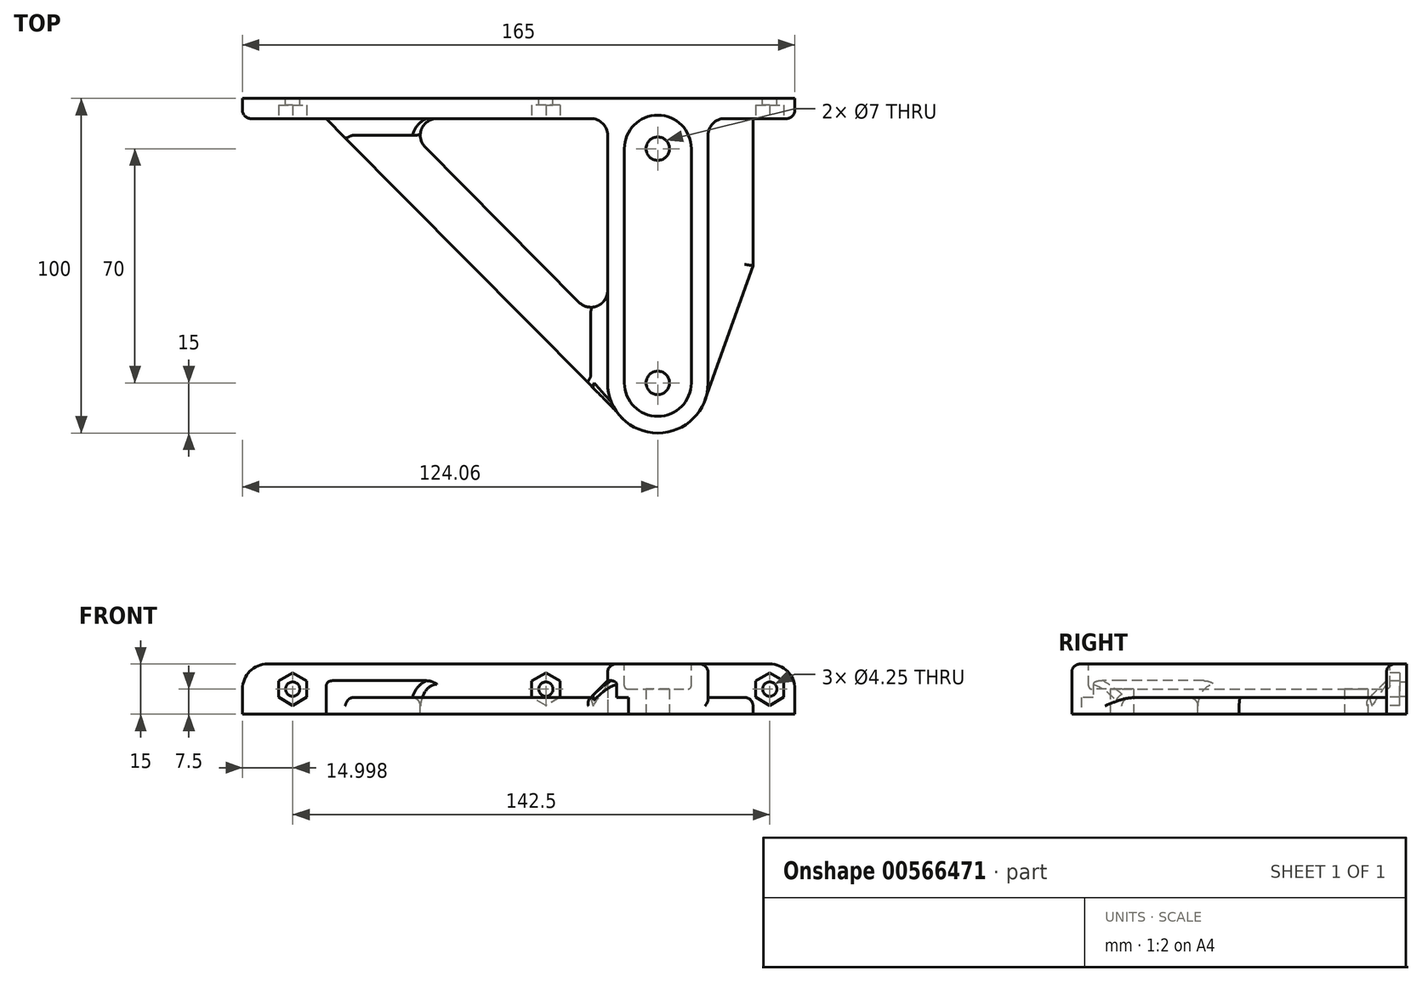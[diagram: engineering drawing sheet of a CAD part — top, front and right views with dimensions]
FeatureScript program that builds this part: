
annotation { "Feature Type Name" : "Feature", "Feature Type Description" : "" }
export const myFeature = defineFeature(function(context is Context, id is Id, definition is map)
    precondition{}
    {
        {
            var Q0;
            Q0=qCreatedBy(makeId("Top.planeOp"),FACE);
            var sketch = newSketch(context, id + "F0", { "sketchPlane" : qUnion([Q0])});
            skLineSegment(sketch, "E0", {"start": v(-124.06, 9) * mm, "end": v(-124.06, 15) * mm});
            skLineSegment(sketch, "E1", {"start": v(-124.06, 15) * mm, "end": v(40.94, 15) * mm});
            skLineSegment(sketch, "E2", {"start": v(40.94, 15) * mm, "end": v(40.94, 9) * mm});
            skLineSegment(sketch, "E3", {"start": v(12.37, -78.48) * mm, "end": v(10, -85) * mm, "construction": true});
            skLineSegment(sketch, "E4", {"start": v(10, -85) * mm, "end": v(-10, -85) * mm, "construction": true});
            skLineSegment(sketch, "E5", {"start": v(-10, -85) * mm, "end": v(-124.06, 0) * mm, "construction": true});
            skCircle(sketch, "E6", {"center": v(0, 0) * mm, "radius": 3.5 * mm});
            skCircle(sketch, "E7", {"center": v(0, -70) * mm, "radius": 3.5 * mm});
            skArc(sketch, "E8", {"start": v(-8.7, -82.22) * mm, "mid": v(4.5, -84.31) * mm, "end": v(14.13, -75.05) * mm});
            skLineSegment(sketch, "E9", {"start": v(28.44, -34.99) * mm, "end": v(14.13, -75.05) * mm});
            skLineSegment(sketch, "E10", {"start": v(-124.06, 0) * mm, "end": v(-8.7, -82.22) * mm, "construction": true});
            skLineSegment(sketch, "E11", {"start": v(-77.95, 9) * mm, "end": v(-15, 9) * mm});
            skLineSegment(sketch, "E12", {"start": v(-15, 9) * mm, "end": v(-15, -54.55) * mm});
            skLineSegment(sketch, "E13", {"start": v(-15, -54.55) * mm, "end": v(-77.95, 9) * mm});
            skLineSegment(sketch, "E14", {"start": v(-124.06, 9) * mm, "end": v(-99.06, 9) * mm});
            skLineSegment(sketch, "E15", {"start": v(-99.06, 9) * mm, "end": v(-8.7, -82.22) * mm});
            skLineSegment(sketch, "E16", {"start": v(28.44, 9) * mm, "end": v(40.94, 9) * mm});
            skLineSegment(sketch, "E17", {"start": v(28.44, 9) * mm, "end": v(28.44, -34.99) * mm});
            skPoint(sketch, "E18.orphan", {"position": v(40.94, 0) * mm});
            skSolve(sketch);
        }
        {
            var Q0;
            Q0=qSketchRegion(id+"F0",true);
            extrude(context, id + "F1", {"entities" : qUnion([Q0]), "depth" : 5 * mm});
        }
        {
            var Q0;
            Q0=makeQuery(id+"F1.opExtrude","CAP_FACE",FACE,{"disambiguationData":[OSD([sQuery(id+"F0.wireOp",EDGE,"E0"),sQuery(id+"F0.wireOp",EDGE,"E1"),sQuery(id+"F0.wireOp",EDGE,"E2"),sQuery(id+"F0.wireOp",EDGE,"E3"),sQuery(id+"F0.wireOp",EDGE,"E4"),sQuery(id+"F0.wireOp",EDGE,"E5"),sQuery(id+"F0.wireOp",EDGE,"E6"),sQuery(id+"F0.wireOp",EDGE,"E7"),sQuery(id+"F0.wireOp",EDGE,"brWuAORZ-QQ3N-mHyy-jjcm-9xjy5NoIPpaN"),sQuery(id+"F0.wireOp",EDGE,"hGYEL4FP-7Z2F-9BLv-NZoW-4O7jBzdm4NG0"),sQuery(id+"F0.wireOp",EDGE,"Ev3Ag6zw-3mFU-VTcE-mw61-bQwCWqHxOj75"),sQuery(id+"F0.wireOp",EDGE,"rvlW2tZY-N1AQ-Yf2F-EbRQ-ggfH0PUhPHp1")])],"isStart":false});
            var sketch = newSketch(context, id + "F2", { "sketchPlane" : qUnion([Q0])});
            skLineSegment(sketch, "E19.bottom", {"start": v(-124.06, 15) * mm, "end": v(40.94, 15) * mm});
            skLineSegment(sketch, "E19.top", {"start": v(-124.06, 9) * mm, "end": v(-15, 9) * mm});
            skLineSegment(sketch, "E19.left", {"start": v(-124.06, 15) * mm, "end": v(-124.06, 9) * mm});
            skLineSegment(sketch, "E19.right", {"start": v(40.94, 15) * mm, "end": v(40.94, 9) * mm});
            skLineSegment(sketch, "E20.left", {"start": v(-15, -70) * mm, "end": v(-15, 9) * mm});
            skLineSegment(sketch, "E20.right", {"start": v(15, -70) * mm, "end": v(15, 9) * mm});
            skLineSegment(sketch, "E21.trimOffspring", {"start": v(15, 9) * mm, "end": v(40.94, 9) * mm});
            skCircle(sketch, "E22", {"center": v(0, 0) * mm, "radius": 3.5 * mm});
            skCircle(sketch, "E23", {"center": v(0, -70) * mm, "radius": 3.5 * mm});
            skArc(sketch, "E24", {"start": v(0, -85) * mm, "mid": v(10.6, -80.6) * mm, "end": v(15, -70) * mm});
            skArc(sketch, "E25.MirrorCS", {"start": v(0, -85) * mm, "mid": v(-10.6, -80.6) * mm, "end": v(-15, -70) * mm});
            skSolve(sketch);
        }
        {
            var Q0;
            Q0=qSketchRegion(id+"F2",true);
            extrude(context, id + "F3", {"entities" : qUnion([Q0]), "operationType" : NewBodyOperationType.ADD, "depth" : 10 * mm});
        }
        {
            var Q0;
            Q0=makeQuery(id+"F3.opExtrude","SWEPT_EDGE",EDGE,{"disambiguationData":[OSD([sQuery(id+"F2.wireOp",EDGE,"E19.top"),sQuery(id+"F2.wireOp",EDGE,"E20.left")])]});
            var Q1;
            Q1=makeQuery(id+"F3.opExtrude","SWEPT_EDGE",EDGE,{"disambiguationData":[OSD([sQuery(id+"F2.wireOp",EDGE,"E20.right"),sQuery(id+"F2.wireOp",EDGE,"E21.trimOffspring")])]});
            fillet(context, id + "F4", {"entities" : qUnion([Q0, Q1]), "radius" : 5 * mm, "tangentPropagation" : true, "allowEdgeOverflow" : false});
        }
        {
            var Q0;
            Q0=makeQuery(id+"F3.boolean.opBoolean","MERGE",FACE,{"derivedFrom":[makeQuery(id+"F1.opExtrude","SWEPT_FACE",FACE,{"disambiguationData":[OSD([sQuery(id+"F0.wireOp",EDGE,"E1")])]}),makeQuery(id+"F3.opExtrude","SWEPT_FACE",FACE,{"disambiguationData":[OSD([sQuery(id+"F2.wireOp",EDGE,"E19.bottom")])]})]});
            var sketch = newSketch(context, id + "F5", { "sketchPlane" : qUnion([Q0])});
            skCircle(sketch, "E26", {"center": v(-33.44, 7.5) * mm, "radius": 2.12 * mm});
            skCircle(sketch, "E27", {"center": v(109.06, 7.5) * mm, "radius": 2.12 * mm});
            skCircle(sketch, "E28.MirrorC", {"center": v(33.44, 7.5) * mm, "radius": 2.12 * mm});
            skSolve(sketch);
        }
        {
            var Q0;
            Q0=qSketchRegion(id+"F5",true);
            extrude(context, id + "F6", {"entities" : qUnion([Q0]), "operationType" : NewBodyOperationType.REMOVE, "oppositeDirection" : true, "depth" : 25 * mm});
        }
        {
            var Q0;
            {var subQ0=sQuery(id+"F0.wireOp",EDGE,"Ev3Ag6zw-3mFU-VTcE-mw61-bQwCWqHxOj75");var subQ1=sQuery(id+"F0.wireOp",EDGE,"hGYEL4FP-7Z2F-9BLv-NZoW-4O7jBzdm4NG0");var subQ2=sQuery(id+"F0.wireOp",EDGE,"rvlW2tZY-N1AQ-Yf2F-EbRQ-ggfH0PUhPHp1");var subQ3=sQuery(id+"F0.wireOp",EDGE,"E0");var subQ4=sQuery(id+"F0.wireOp",EDGE,"E8");var subQ5=sQuery(id+"F0.wireOp",EDGE,"E10");var subQ6=sQuery(id+"F2.wireOp",EDGE,"E19.top");var subQ7=sQuery(id+"F2.wireOp",EDGE,"E20.left");Q0=makeQuery(id+"F4.opFillet","BLEND_EDGE",EDGE,{"blendedFrom":[makeQuery(id+"F3.opExtrude","SWEPT_EDGE",EDGE,{"disambiguationData":[OSD([subQ6,subQ7])]}),makeQuery(id+"F3.boolean.opBoolean","SPLIT",FACE,{"disambiguationData":[TD([makeQuery(id+"F1.opExtrude","SWEPT_FACE",FACE,{"disambiguationData":[OSD([subQ3])]})])],"derivedFrom":makeQuery(id+"F1.opExtrude","CAP_FACE",FACE,{"disambiguationData":[OSD([subQ3,sQuery(id+"F0.wireOp",EDGE,"E1"),sQuery(id+"F0.wireOp",EDGE,"E2"),sQuery(id+"F0.wireOp",EDGE,"E6"),sQuery(id+"F0.wireOp",EDGE,"E7"),sQuery(id+"F0.wireOp",EDGE,"brWuAORZ-QQ3N-mHyy-jjcm-9xjy5NoIPpaN"),subQ1,subQ0,subQ2,subQ4,sQuery(id+"F0.wireOp",EDGE,"E9"),subQ5])],"isStart":false})})],"blendedInto":[makeQuery(id+"F3.boolean.opBoolean","SPLIT",FACE,{"disambiguationData":[TD([makeQuery(id+"F1.opExtrude","SWEPT_FACE",FACE,{"disambiguationData":[OSD([subQ3])]})])],"derivedFrom":makeQuery(id+"F1.opExtrude","CAP_FACE",FACE,{"disambiguationData":[OSD([subQ3,sQuery(id+"F0.wireOp",EDGE,"E1"),sQuery(id+"F0.wireOp",EDGE,"E2"),sQuery(id+"F0.wireOp",EDGE,"E6"),sQuery(id+"F0.wireOp",EDGE,"E7"),sQuery(id+"F0.wireOp",EDGE,"brWuAORZ-QQ3N-mHyy-jjcm-9xjy5NoIPpaN"),subQ1,subQ0,subQ2,subQ4,sQuery(id+"F0.wireOp",EDGE,"E9"),subQ5])],"isStart":false})})]});}
            var Q1;
            {var subQ0=sQuery(id+"F0.wireOp",EDGE,"E8");var subQ1=sQuery(id+"F0.wireOp",EDGE,"E9");var subQ2=sQuery(id+"F0.wireOp",EDGE,"brWuAORZ-QQ3N-mHyy-jjcm-9xjy5NoIPpaN");var subQ3=sQuery(id+"F0.wireOp",EDGE,"E2");var subQ4=sQuery(id+"F2.wireOp",EDGE,"E20.right");var subQ5=sQuery(id+"F2.wireOp",EDGE,"E21.trimOffspring");Q1=makeQuery(id+"F4.opFillet","BLEND_EDGE",EDGE,{"blendedFrom":[makeQuery(id+"F3.opExtrude","SWEPT_EDGE",EDGE,{"disambiguationData":[OSD([subQ4,subQ5])]}),makeQuery(id+"F3.boolean.opBoolean","SPLIT",FACE,{"disambiguationData":[TD([makeQuery(id+"F1.opExtrude","SWEPT_FACE",FACE,{"disambiguationData":[OSD([subQ3])]})])],"derivedFrom":makeQuery(id+"F1.opExtrude","CAP_FACE",FACE,{"disambiguationData":[OSD([sQuery(id+"F0.wireOp",EDGE,"E0"),sQuery(id+"F0.wireOp",EDGE,"E1"),subQ3,sQuery(id+"F0.wireOp",EDGE,"E6"),sQuery(id+"F0.wireOp",EDGE,"E7"),subQ2,sQuery(id+"F0.wireOp",EDGE,"hGYEL4FP-7Z2F-9BLv-NZoW-4O7jBzdm4NG0"),sQuery(id+"F0.wireOp",EDGE,"Ev3Ag6zw-3mFU-VTcE-mw61-bQwCWqHxOj75"),sQuery(id+"F0.wireOp",EDGE,"rvlW2tZY-N1AQ-Yf2F-EbRQ-ggfH0PUhPHp1"),subQ0,subQ1,sQuery(id+"F0.wireOp",EDGE,"E10")])],"isStart":false})})],"blendedInto":[makeQuery(id+"F3.boolean.opBoolean","SPLIT",FACE,{"disambiguationData":[TD([makeQuery(id+"F1.opExtrude","SWEPT_FACE",FACE,{"disambiguationData":[OSD([subQ3])]})])],"derivedFrom":makeQuery(id+"F1.opExtrude","CAP_FACE",FACE,{"disambiguationData":[OSD([sQuery(id+"F0.wireOp",EDGE,"E0"),sQuery(id+"F0.wireOp",EDGE,"E1"),subQ3,sQuery(id+"F0.wireOp",EDGE,"E6"),sQuery(id+"F0.wireOp",EDGE,"E7"),subQ2,sQuery(id+"F0.wireOp",EDGE,"hGYEL4FP-7Z2F-9BLv-NZoW-4O7jBzdm4NG0"),sQuery(id+"F0.wireOp",EDGE,"Ev3Ag6zw-3mFU-VTcE-mw61-bQwCWqHxOj75"),sQuery(id+"F0.wireOp",EDGE,"rvlW2tZY-N1AQ-Yf2F-EbRQ-ggfH0PUhPHp1"),subQ0,subQ1,sQuery(id+"F0.wireOp",EDGE,"E10")])],"isStart":false})})]});}
            var Q2;
            Q2=makeQuery(id+"F3.opExtrude","CAP_EDGE",EDGE,{"disambiguationData":[OSD([sQuery(id+"F2.wireOp",EDGE,"E20.left")])],"isStart":true});
            var Q3;
            Q3=makeQuery(id+"F3.opExtrude","CAP_EDGE",EDGE,{"disambiguationData":[OSD([sQuery(id+"F2.wireOp",EDGE,"E19.top")])],"isStart":true});
            var Q4;
            Q4=makeQuery(id+"F3.opExtrude","CAP_EDGE",EDGE,{"disambiguationData":[OSD([sQuery(id+"F2.wireOp",EDGE,"E21.trimOffspring")])],"isStart":true});
            chamfer(context, id + "F7", {"entities" : qUnion([Q0, Q1, Q2, Q3, Q4]), "width" : 5 * mm, "tangentPropagation" : true});
        }
        {
            var Q0;
            Q0=makeQuery(id+"F1.opExtrude","SWEPT_EDGE",EDGE,{"disambiguationData":[OSD([sQuery(id+"F0.wireOp",EDGE,"E12"),sQuery(id+"F0.wireOp",EDGE,"E13")])]});
            var Q1;
            Q1=makeQuery(id+"F1.opExtrude","SWEPT_EDGE",EDGE,{"disambiguationData":[OSD([sQuery(id+"F0.wireOp",EDGE,"E11"),sQuery(id+"F0.wireOp",EDGE,"E12")])]});
            var Q2;
            Q2=makeQuery(id+"F1.opExtrude","SWEPT_EDGE",EDGE,{"disambiguationData":[OSD([sQuery(id+"F0.wireOp",EDGE,"E11"),sQuery(id+"F0.wireOp",EDGE,"E13")])]});
            fillet(context, id + "F8", {"entities" : qUnion([Q0, Q1, Q2]), "radius" : 5 * mm, "tangentPropagation" : true, "allowEdgeOverflow" : false});
        }
        {
            var Q0;
            Q0=makeQuery(id+"F3.opExtrude","CAP_FACE",FACE,{"disambiguationData":[OSD([sQuery(id+"F2.wireOp",EDGE,"E19.bottom"),sQuery(id+"F2.wireOp",EDGE,"E19.top"),sQuery(id+"F2.wireOp",EDGE,"E19.left"),sQuery(id+"F2.wireOp",EDGE,"E19.right"),sQuery(id+"F2.wireOp",EDGE,"E20.left"),sQuery(id+"F2.wireOp",EDGE,"E20.right"),sQuery(id+"F2.wireOp",EDGE,"E21.trimOffspring"),sQuery(id+"F2.wireOp",EDGE,"E22"),sQuery(id+"F2.wireOp",EDGE,"E23"),sQuery(id+"F2.wireOp",EDGE,"E24"),sQuery(id+"F2.wireOp",EDGE,"E25.MirrorCS")])],"isStart":false});
            var sketch = newSketch(context, id + "F9", { "sketchPlane" : qUnion([Q0])});
            skLineSegment(sketch, "E29.bottom", {"start": v(0, -80) * mm, "end": v(0, -80) * mm});
            skLineSegment(sketch, "E29.top", {"start": v(0, 10) * mm, "end": v(0, 10) * mm});
            skLineSegment(sketch, "E29.left", {"start": v(10, -70) * mm, "end": v(10, 0) * mm});
            skLineSegment(sketch, "E29.right", {"start": v(-10, -70) * mm, "end": v(-10, 0) * mm});
            skPoint(sketch, "E29.middle", {"position": v(0, -35) * mm});
            skPoint(sketch, "E30.visualSharp", {"position": v(-10, 10) * mm});
            skArc(sketch, "E30.filletArc", {"start": v(0, 10) * mm, "mid": v(-7.07, 7.07) * mm, "end": v(-10, 0) * mm});
            skPoint(sketch, "E31.visualSharp", {"position": v(10, 10) * mm});
            skArc(sketch, "E31.filletArc", {"start": v(10, 0) * mm, "mid": v(7.07, 7.07) * mm, "end": v(0, 10) * mm});
            skPoint(sketch, "E32.visualSharp", {"position": v(10, -80) * mm});
            skArc(sketch, "E32.filletArc", {"start": v(0, -80) * mm, "mid": v(7.07, -77.07) * mm, "end": v(10, -70) * mm});
            skPoint(sketch, "E33.visualSharp", {"position": v(-10, -80) * mm});
            skArc(sketch, "E33.filletArc", {"start": v(-10, -70) * mm, "mid": v(-7.07, -77.07) * mm, "end": v(0, -80) * mm});
            skSolve(sketch);
        }
        {
            var Q0;
            Q0=qSketchRegion(id+"F9",true);
            extrude(context, id + "F10", {"entities" : qUnion([Q0]), "operationType" : NewBodyOperationType.REMOVE, "oppositeDirection" : true, "depth" : 7.5 * mm});
        }
        {
            var Q0;
            Q0=makeQuery(id+"F3.opExtrude","CAP_EDGE",EDGE,{"disambiguationData":[OSD([sQuery(id+"F2.wireOp",EDGE,"E19.right")])],"isStart":false});
            var Q1;
            Q1=makeQuery(id+"F3.opExtrude","CAP_EDGE",EDGE,{"disambiguationData":[OSD([sQuery(id+"F2.wireOp",EDGE,"E19.left")])],"isStart":false});
            fillet(context, id + "F11", {"entities" : qUnion([Q0, Q1]), "radius" : 7.5 * mm, "tangentPropagation" : true, "allowEdgeOverflow" : false});
        }
        {
            var Q0;
            Q0=makeQuery(id+"F3.opExtrude","CAP_EDGE",EDGE,{"disambiguationData":[OSD([sQuery(id+"F2.wireOp",EDGE,"E20.left")])],"isStart":false});
            var Q1;
            Q1=makeQuery(id+"F1.opExtrude","CAP_EDGE",EDGE,{"disambiguationData":[OSD([sQuery(id+"F0.wireOp",EDGE,"E9")])],"isStart":false});
            var Q2;
            Q2=makeQuery(id+"F1.opExtrude","CAP_EDGE",EDGE,{"disambiguationData":[OSD([sQuery(id+"F0.wireOp",EDGE,"E17")])],"isStart":false});
            var Q3;
            {var subQ0=sQuery(id+"F0.wireOp",EDGE,"E15");Q3=makeQuery(id+"F3.boolean.opBoolean","SPLIT",EDGE,{"disambiguationData":[topologyDisambiguationEdgeConnected([makeQuery(id+"F1.opExtrude","CAP_FACE",FACE,{"disambiguationData":[OSD([sQuery(id+"F0.wireOp",EDGE,"E0"),sQuery(id+"F0.wireOp",EDGE,"E1"),sQuery(id+"F0.wireOp",EDGE,"E2"),sQuery(id+"F0.wireOp",EDGE,"E6"),sQuery(id+"F0.wireOp",EDGE,"E7"),sQuery(id+"F0.wireOp",EDGE,"E8"),sQuery(id+"F0.wireOp",EDGE,"E9"),sQuery(id+"F0.wireOp",EDGE,"E11"),sQuery(id+"F0.wireOp",EDGE,"E12"),sQuery(id+"F0.wireOp",EDGE,"E13"),sQuery(id+"F0.wireOp",EDGE,"E14"),subQ0,sQuery(id+"F0.wireOp",EDGE,"E16"),sQuery(id+"F0.wireOp",EDGE,"E17")])],"isStart":false})])],"derivedFrom":makeQuery(id+"F1.opExtrude","CAP_EDGE",EDGE,{"disambiguationData":[OSD([subQ0])],"isStart":false})});}
            var Q4;
            Q4=makeQuery(id+"F1.opExtrude","CAP_EDGE",EDGE,{"disambiguationData":[OSD([sQuery(id+"F0.wireOp",EDGE,"E13")])],"isStart":false});
            var Q5;
            Q5=makeQuery(id+"F10.boolean.opBoolean","COPY",EDGE,{"derivedFrom":makeQuery(id+"F10.opExtrude","CAP_EDGE",EDGE,{"disambiguationData":[OSD([sQuery(id+"F9.wireOp",EDGE,"E30.filletArc"),sQuery(id+"F9.wireOp",EDGE,"E31.filletArc")])],"isStart":true})});
            var Q6;
            Q6=makeQuery(id+"F7.opChamfer","BLEND_EDGE",EDGE,{"blendedFrom":[makeQuery(id+"F3.opExtrude","CAP_EDGE",EDGE,{"disambiguationData":[OSD([sQuery(id+"F2.wireOp",EDGE,"E19.top")])],"isStart":true}),makeQuery(id+"F1.opExtrude","SWEPT_FACE",FACE,{"disambiguationData":[OSD([sQuery(id+"F0.wireOp",EDGE,"E15")])]})],"blendedInto":[makeQuery(id+"F1.opExtrude","SWEPT_FACE",FACE,{"disambiguationData":[OSD([sQuery(id+"F0.wireOp",EDGE,"E15")])]})]});
            var Q7;
            Q7=makeQuery(id+"F8.opFillet","BLEND_EDGE",EDGE,{"blendedFrom":[makeQuery(id+"F1.opExtrude","SWEPT_EDGE",EDGE,{"disambiguationData":[OSD([sQuery(id+"F0.wireOp",EDGE,"E11"),sQuery(id+"F0.wireOp",EDGE,"E13")])]}),makeQuery(id+"F7.opChamfer","BLEND_FACE",FACE,{"disambiguationData":[OSD([sQuery(id+"F2.wireOp",EDGE,"E19.top")])]})],"blendedInto":[makeQuery(id+"F7.opChamfer","BLEND_FACE",FACE,{"disambiguationData":[OSD([sQuery(id+"F2.wireOp",EDGE,"E19.top")])]})]});
            var Q8;
            Q8=makeQuery(id+"F7.opChamfer","BLEND_EDGE",EDGE,{"blendedFrom":[makeQuery(id+"F3.opExtrude","CAP_EDGE",EDGE,{"disambiguationData":[OSD([sQuery(id+"F2.wireOp",EDGE,"E21.trimOffspring")])],"isStart":true}),makeQuery(id+"F1.opExtrude","SWEPT_FACE",FACE,{"disambiguationData":[OSD([sQuery(id+"F0.wireOp",EDGE,"E17")])]})],"blendedInto":[makeQuery(id+"F1.opExtrude","SWEPT_FACE",FACE,{"disambiguationData":[OSD([sQuery(id+"F0.wireOp",EDGE,"E17")])]})]});
            var Q9;
            {var subQ0=sQuery(id+"F0.wireOp",EDGE,"E15");var subQ1=makeQuery(id+"F1.opExtrude","SWEPT_FACE",FACE,{"disambiguationData":[OSD([subQ0])]});var subQ2=sQuery(id+"F0.wireOp",EDGE,"E12");var subQ3=sQuery(id+"F0.wireOp",EDGE,"E8");var subQ4=makeQuery(id+"F1.opExtrude","CAP_FACE",FACE,{"disambiguationData":[OSD([sQuery(id+"F0.wireOp",EDGE,"E0"),sQuery(id+"F0.wireOp",EDGE,"E1"),sQuery(id+"F0.wireOp",EDGE,"E2"),sQuery(id+"F0.wireOp",EDGE,"E6"),sQuery(id+"F0.wireOp",EDGE,"E7"),subQ3,sQuery(id+"F0.wireOp",EDGE,"E9"),sQuery(id+"F0.wireOp",EDGE,"E11"),subQ2,sQuery(id+"F0.wireOp",EDGE,"E13"),sQuery(id+"F0.wireOp",EDGE,"E14"),subQ0,sQuery(id+"F0.wireOp",EDGE,"E16"),sQuery(id+"F0.wireOp",EDGE,"E17")])],"isStart":false});var subQ5=sQuery(id+"F2.wireOp",EDGE,"E25.MirrorCS");var subQ6=sQuery(id+"F2.wireOp",EDGE,"E24");var subQ8=makeQuery(id+"F1.opExtrude","SWEPT_FACE",FACE,{"disambiguationData":[OSD([subQ3])]});var subQ9=makeQuery(id+"F3.opExtrude","SWEPT_FACE",FACE,{"disambiguationData":[OSD([subQ6,subQ5])]});Q9=makeQuery(id+"F7.opChamfer","BLEND_EDGE",EDGE,{"blendedFrom":[makeQuery(id+"F3.boolean.opBoolean","SPLIT",EDGE,{"disambiguationData":[topologyDisambiguationEdgeConnected([subQ4,subQ8,subQ9]),TD([makeQuery(id+"F1.opExtrude","SWEPT_FACE",FACE,{"disambiguationData":[OSD([subQ2])]})])],"derivedFrom":makeQuery(id+"F3.opExtrude","CAP_EDGE",EDGE,{"disambiguationData":[OSD([subQ6,subQ5])],"isStart":true})}),subQ1],"blendedInto":[subQ1]});}
            var Q10;
            Q10=makeQuery(id+"F8.opFillet","BLEND_EDGE",EDGE,{"blendedFrom":[makeQuery(id+"F1.opExtrude","SWEPT_EDGE",EDGE,{"disambiguationData":[OSD([sQuery(id+"F0.wireOp",EDGE,"E12"),sQuery(id+"F0.wireOp",EDGE,"E13")])]}),makeQuery(id+"F7.opChamfer","BLEND_FACE",FACE,{"disambiguationData":[OSD([sQuery(id+"F2.wireOp",EDGE,"E20.left")])]})],"blendedInto":[makeQuery(id+"F7.opChamfer","BLEND_FACE",FACE,{"disambiguationData":[OSD([sQuery(id+"F2.wireOp",EDGE,"E20.left")])]})]});
            fillet(context, id + "F12", {"entities" : qUnion([Q0, Q1, Q2, Q3, Q4, Q5, Q6, Q7, Q8, Q9, Q10]), "radius" : 2.5 * mm, "tangentPropagation" : true, "allowEdgeOverflow" : false});
        }
        {
            var Q0;
            Q0=makeQuery(id+"F10.boolean.opBoolean","COPY",EDGE,{"derivedFrom":makeQuery(id+"F10.opExtrude","CAP_EDGE",EDGE,{"disambiguationData":[OSD([sQuery(id+"F9.wireOp",EDGE,"E30.filletArc"),sQuery(id+"F9.wireOp",EDGE,"E31.filletArc")])],"isStart":false})});
            fillet(context, id + "F13", {"entities" : qUnion([Q0]), "radius" : 1 * mm, "tangentPropagation" : true, "allowEdgeOverflow" : false});
        }
        {
            var Q0;
            Q0=makeQuery(id+"F3.boolean.opBoolean","MERGE",FACE,{"derivedFrom":[makeQuery(id+"F1.opExtrude","SWEPT_FACE",FACE,{"disambiguationData":[OSD([sQuery(id+"F0.wireOp",EDGE,"E11")])]}),makeQuery(id+"F1.opExtrude","SWEPT_FACE",FACE,{"disambiguationData":[OSD([sQuery(id+"F0.wireOp",EDGE,"E14")])]}),makeQuery(id+"F3.opExtrude","SWEPT_FACE",FACE,{"disambiguationData":[OSD([sQuery(id+"F2.wireOp",EDGE,"E19.top")])]})]});
            var sketch = newSketch(context, id + "F14", { "sketchPlane" : qUnion([Q0])});
            skCircle(sketch, "E34.cCircle", {"center": v(-109.06, 7.5) * mm, "radius": 4.22 * mm, "construction": true});
            skLineSegment(sketch, "E34.0", {"start": v(-104.84, 9.94) * mm, "end": v(-104.84, 5.06) * mm});
            skLineSegment(sketch, "E34.1", {"start": v(-104.84, 5.06) * mm, "end": v(-109.06, 2.62) * mm});
            skLineSegment(sketch, "E34.2", {"start": v(-109.06, 2.62) * mm, "end": v(-113.29, 5.06) * mm});
            skLineSegment(sketch, "E34.3", {"start": v(-113.29, 5.06) * mm, "end": v(-113.29, 9.94) * mm});
            skLineSegment(sketch, "E34.4", {"start": v(-113.29, 9.94) * mm, "end": v(-109.06, 12.38) * mm});
            skLineSegment(sketch, "E34.5", {"start": v(-109.06, 12.38) * mm, "end": v(-104.84, 9.94) * mm});
            skPoint(sketch, "E34.0.midPoint", {"position": v(-104.84, 7.5) * mm});
            skCircle(sketch, "E35.cCircle", {"center": v(-33.44, 7.5) * mm, "radius": 4.22 * mm, "construction": true});
            skLineSegment(sketch, "E35.0", {"start": v(-37.66, 5.06) * mm, "end": v(-37.66, 9.94) * mm});
            skLineSegment(sketch, "E35.1", {"start": v(-37.66, 9.94) * mm, "end": v(-33.44, 12.38) * mm});
            skLineSegment(sketch, "E35.2", {"start": v(-33.44, 12.38) * mm, "end": v(-29.21, 9.94) * mm});
            skLineSegment(sketch, "E35.3", {"start": v(-29.21, 9.94) * mm, "end": v(-29.21, 5.06) * mm});
            skLineSegment(sketch, "E35.4", {"start": v(-29.21, 5.06) * mm, "end": v(-33.44, 2.62) * mm});
            skLineSegment(sketch, "E35.5", {"start": v(-33.44, 2.62) * mm, "end": v(-37.66, 5.06) * mm});
            skPoint(sketch, "E35.0.midPoint", {"position": v(-37.66, 7.5) * mm});
            skCircle(sketch, "E36.cCircle", {"center": v(33.44, 7.5) * mm, "radius": 4.22 * mm, "construction": true});
            skLineSegment(sketch, "E36.0", {"start": v(37.66, 9.94) * mm, "end": v(37.66, 5.06) * mm});
            skLineSegment(sketch, "E36.1", {"start": v(37.66, 5.06) * mm, "end": v(33.44, 2.62) * mm});
            skLineSegment(sketch, "E36.2", {"start": v(33.44, 2.62) * mm, "end": v(29.21, 5.06) * mm});
            skLineSegment(sketch, "E36.3", {"start": v(29.21, 5.06) * mm, "end": v(29.21, 9.94) * mm});
            skLineSegment(sketch, "E36.4", {"start": v(29.21, 9.94) * mm, "end": v(33.44, 12.38) * mm});
            skLineSegment(sketch, "E36.5", {"start": v(33.44, 12.38) * mm, "end": v(37.66, 9.94) * mm});
            skPoint(sketch, "E36.0.midPoint", {"position": v(37.66, 7.5) * mm});
            skSolve(sketch);
        }
        {
            var Q0;
            Q0=qSketchRegion(id+"F14",true);
            extrude(context, id + "F15", {"entities" : qUnion([Q0]), "operationType" : NewBodyOperationType.REMOVE, "oppositeDirection" : true, "depth" : 4 * mm, "offsetDistance" : 25 * mm});
        }
    });
